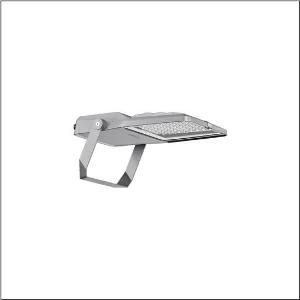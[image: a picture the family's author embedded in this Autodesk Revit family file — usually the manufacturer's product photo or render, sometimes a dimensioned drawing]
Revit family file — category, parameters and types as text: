
# Revit family: floodlight_fl_21_mini___pl33t_5xa7776c2f1a_ac63
name_source: partatom
category: Lighting Fixtures
units: mm (PartAtom-declared; Revit-internal decimal feet)

## family parameters
Cut with Voids When Loaded = No
Host = Face
Light Source = No
Part Type = Normal
Room Calculation Point = No
Round Connector Dimension = Use Diameter
Shared = No

## types (1)
- --- (1 x LED, 12050 lm, 89 W, 3000K)
    Apparent Load = 89 VA
    CIE Flux Codes = 26 75 99 100 100
    Color Rendering = 70
    Color Temperature = 3000K
    Default Elevation = 1800 mm
    Description = Floodlight FL 21 mini, floodlight, primary light control with lens, of PMMA, primary optical cover: protective disc, of toughened safety glass, transparent, light distribution: PL33T, light emission: direct distribution, installation type: surface-mounted, LED, High Power LED, rated luminous flux: 12.050lm, luminous efficacy: 135lm/W, light colour: 730, colour temperature: 3000K, control: flexible luminous flux parameterisation, time-dependent luminous flux control, constant luminous flux control, overheat protection, presetting dimming logarithmic, with terminal, 6-pole, mains connection: 220..240V, AC, 50/60Hz, start of lifetime: 89W, end of service life: 94W, reduction: 43W, luminaire housing, of diecast aluminium, powder-coated, Siteco® metallic grey (DB 702S), corrosivity category C5 mid according to DIN EN ISO 12944, sealing non-destructively replaceable, mounting bracket, of steel, galvanised, powder-coated, Siteco® metallic grey (DB 702S), Smart Interface below and above, protection rating (complete): IP66, insulation class (complete): insulation class II (safety insulation), certification: CE, ENEC, VDE, protection symbol: D, impact resistance: IK08, permissible operating ambient temperature: -40..+40°C, permissible operating ambient temperature for outdoor applications: -40..+50°C, standard: DIN EN 12944, LABS conformity tested according to VDMA 24364:2018-05, packaging unit: 1 piece

Light Distribution: PL33T
    Height = 70 mm
    Lamp = 1 x LED
    Lamp Light Flux = 12050 lm
    Lamp Power = 89 W
    Lamp count = 1
    Length = 485 mm
    Luminous efficacy = 135 lm/W
    Manufacturer = Siteco
    ModVariant = No
    Model = 5XA7776C2F1A
    Number of Poles = 1
    OnlyDefault = Yes
    Power Factor = 1
    Product Name = Floodlight FL 21 mini | PL33T
    Product group = floodlight | pylon annexe
    ProductGroupID = 6200
    Protection Class = Protection class II
    Protection Degree = IP 66
    RLX_Detail_Level = 1
    RLX_Emergency_Light_Flux = 0 lm
    RLX_Emergency_Type = 0
    RLX_Emergency_Type_DB = No
    RlxData = <blob elided: 95741 chars, md5=4a40ee74>
    Socket = socket
    Standby Power = 0 W
    System Light Flux = 12050 lm
    System Power = 89 W
    Type Comments = factory setting: luminous flux: 100 % | dim-lin: 254 | 456 mA
    Type Image = l_1006845.jpg
    URL = http://relux.com
    VarID = @adj_080993
    Voltage = 0 V
    Weight = 0.00 kg
    Width = 337 mm

## geometry (parser evidence)
native form markers: Blend x4, Sweep x12
no freeform markers — native parametric forms only
